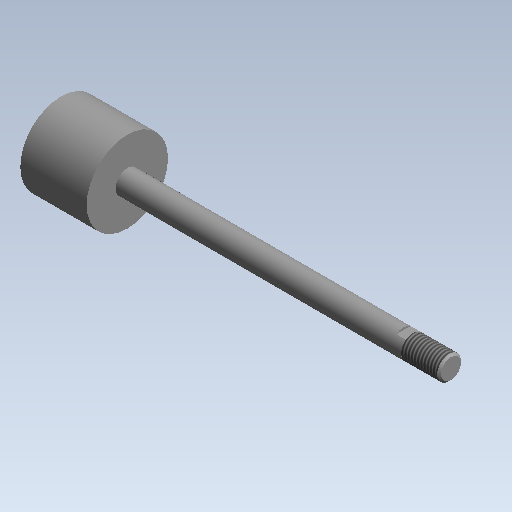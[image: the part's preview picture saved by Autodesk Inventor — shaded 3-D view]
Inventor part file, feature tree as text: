
AUTODESK INVENTOR PART (.ipt)
format: ipt  version: 2020 (Build 240168000, 168)  size: 161,792 bytes
history: native  units: mm (DEFAULTED — no unit token found)
features: other x98, sketch x3, revolve x2, thread x1, extrude x1
ambient origin geometry x8: Origin, YZ Plane, XZ Plane, XY Plane, X Axis, Y Axis, Z Axis, Center Point
bodies: Solid1 (feature_tree)
feature tree (105):
  revolve  "Revolution1"  Angle=360.0deg
  revolve  "Revolution2"  [1 undecoded]
  thread  "Thread1"  [1 undecoded]
  extrude  "Extrusion1"  [1 undecoded]
  other  "dia1_XY"
  other  "dia1_YZ"
  other  "dia1_ZX"
  other  "dia1_X"
  other  "dia1_Y"
  other  "dia1_Z"
  other  "dia1_Center"
  other  "dia12_XY"
  other  "dia12_YZ"
  other  "dia12_ZX"
  other  "dia12_X"
  other  "dia12_Y"
  other  "dia12_Z"
  other  "dia12_Center"
  other  "dia2_XY"
  other  "dia2_YZ"
  other  "dia2_ZX"
  other  "dia2_X"
  other  "dia2_Y"
  other  "dia2_Z"
  other  "dia2_Center"
  other  "dia22_XY"
  other  "dia22_YZ"
  other  "dia22_ZX"
  other  "dia22_X"
  other  "dia22_Y"
  other  "dia22_Z"
  other  "dia22_Center"
  other  "rl1_XY"
  other  "rl1_YZ"
  other  "rl1_ZX"
  other  "rl1_X"
  other  "rl1_Y"
  other  "rl1_Z"
  other  "rl1_Center"
  other  "rl2_XY"
  other  "rl2_YZ"
  other  "rl2_ZX"
  other  "rl2_X"
  other  "rl2_Y"
  other  "rl2_Z"
  other  "rl2_Center"
  other  "rod_cp_XY"
  other  "rod_cp_YZ"
  other  "rod_cp_ZX"
  other  "rod_cp_X"
  other  "rod_cp_Y"
  other  "rod_cp_Z"
  other  "rod_cp_Center"
  other  "thd1_XY"
  other  "thd1_YZ"
  other  "thd1_ZX"
  other  "thd1_X"
  other  "thd1_Y"
  other  "thd1_Z"
  other  "thd1_Center"
  other  "thd2_XY"
  other  "thd2_YZ"
  other  "thd2_ZX"
  other  "thd2_X"
  other  "thd2_Y"
  other  "thd2_Z"
  other  "thd2_Center"
  other  "to_rod_clevis_XY"
  other  "to_rod_clevis_YZ"
  other  "to_rod_clevis_ZX"
  other  "to_rod_clevis_X"
  other  "to_rod_clevis_Y"
  other  "to_rod_clevis_Z"
  other  "to_rod_clevis_Center"
  other  "wf1_XY"
  other  "wf1_YZ"
  other  "wf1_ZX"
  other  "wf1_X"
  other  "wf1_Y"
  other  "wf1_Z"
  other  "wf1_Center"
  other  "wf2_XY"
  other  "wf2_YZ"
  other  "wf2_ZX"
  other  "wf2_X"
  other  "wf2_Y"
  other  "wf2_Z"
  other  "wf2_Center"
  other  "wfw1_XY"
  other  "wfw1_YZ"
  other  "wfw1_ZX"
  other  "wfw1_X"
  other  "wfw1_Y"
  other  "wfw1_Z"
  other  "wfw1_Center"
  other  "wfw2_XY"
  other  "wfw2_YZ"
  other  "wfw2_ZX"
  other  "wfw2_X"
  other  "wfw2_Y"
  other  "wfw2_Z"
  other  "wfw2_Center"
  sketch  "Sketch_1"  dims[d0=360.0deg d1=360.0deg]
  sketch  "Sketch_3"  dims[d2=12.0701mm d3=0.0mm d4=3.175mm d5=0.0mm]
  sketch  "Sketch_10"  dims[d6=0.0mm d7=0.0mm d8=0.0mm d9=0.0mm d10=0.0mm d11=0.0mm d12=0.0mm]
note: 3 required parameter values undecoded (feature->parameter linkage not recoverable at this tier; creation-order binding heuristic only, values carry confidence <= 0.55)